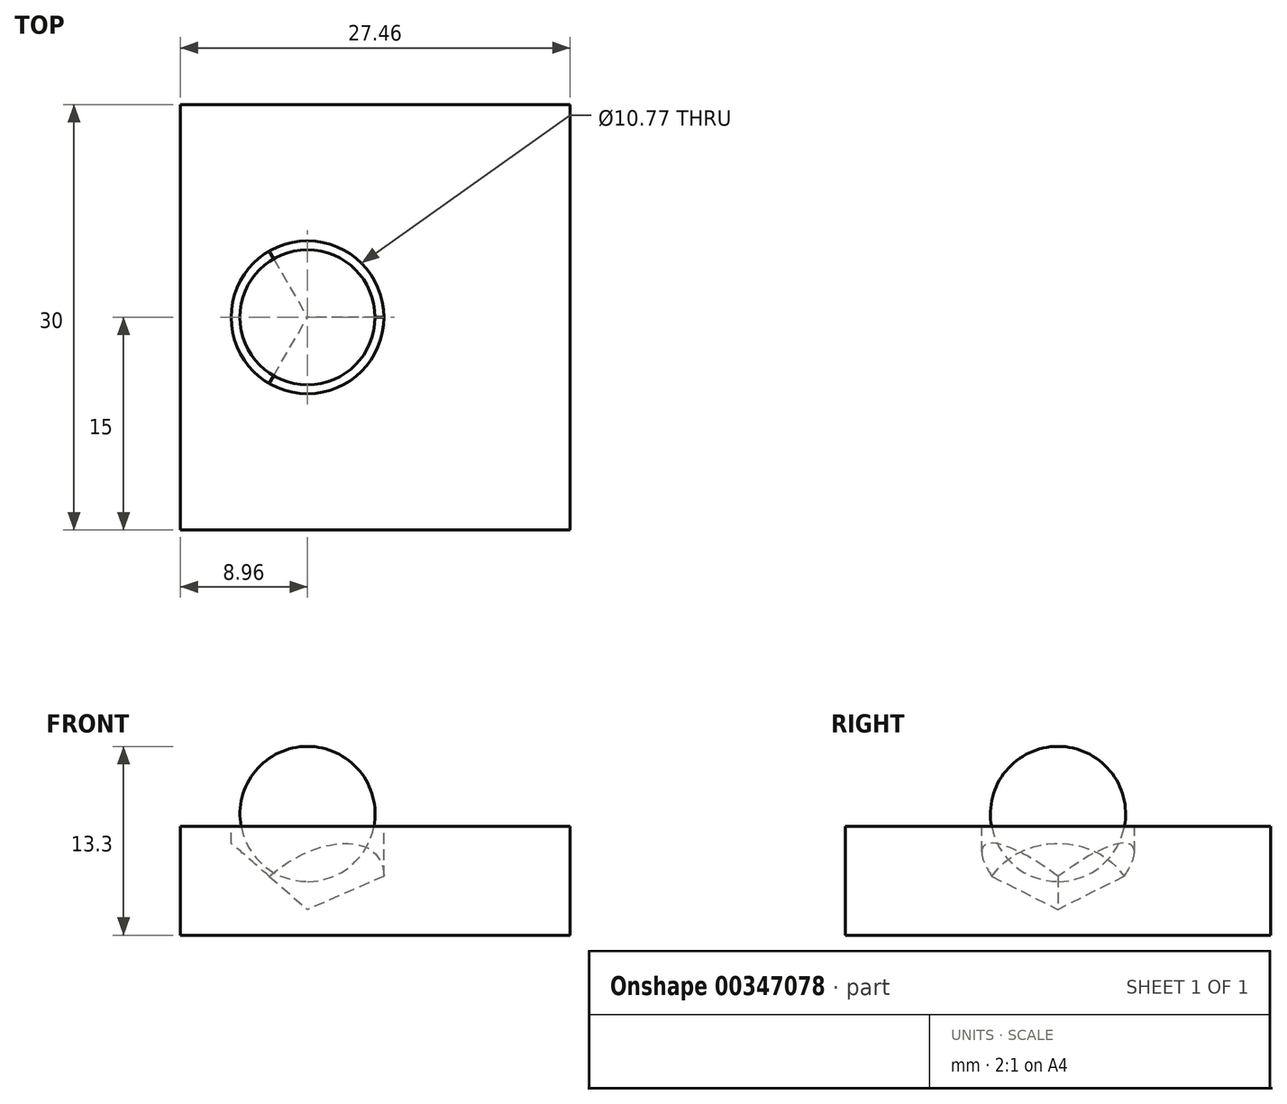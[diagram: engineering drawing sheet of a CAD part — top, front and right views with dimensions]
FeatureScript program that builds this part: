
annotation { "Feature Type Name" : "Feature", "Feature Type Description" : "" }
export const myFeature = defineFeature(function(context is Context, id is Id, definition is map)
    precondition{}
    {
        {
            var Q0;
            Q0=qCreatedBy(makeId("Front.planeOp"),FACE);
            var sketch = newSketch(context, id + "F0", { "sketchPlane" : qUnion([Q0])});
            skLineSegment(sketch, "E0", {"start": v(-6.74, 4.43) * mm, "end": v(0, -2.3) * mm});
            skLineSegment(sketch, "E1", {"start": v(-6.74, 4.43) * mm, "end": v(0, 4.43) * mm});
            skLineSegment(sketch, "E2", {"start": v(0, 4.43) * mm, "end": v(0, -0.33) * mm});
            skPoint(sketch, "E3", {"position": v(-4.76, 4.43) * mm});
            skLineSegment(sketch, "E4", {"start": v(0, -0.33) * mm, "end": v(0, -2.3) * mm});
            skLineSegment(sketch, "E5", {"start": v(0, 4.43) * mm, "end": v(0, 9.2) * mm});
            skLineSegment(sketch, "E6", {"start": v(0, 9.2) * mm, "end": v(0, 12.63) * mm, "construction": true});
            skArc(sketch, "E7", {"start": v(0, 9.2) * mm, "mid": v(-4.76, 4.43) * mm, "end": v(0, -0.33) * mm, "construction": true});
            skArc(sketch, "E8", {"start": v(0, -0.33) * mm, "mid": v(4.76, 4.43) * mm, "end": v(0, 9.2) * mm});
            skSolve(sketch);
        }
        {
            var Q0;
            Q0=qCreatedBy(makeId("Front.planeOp"),FACE);
            var sketch = newSketch(context, id + "F1", { "sketchPlane" : qUnion([Q0])});
            skLineSegment(sketch, "E9.bottom", {"start": v(-8.96, 3.55) * mm, "end": v(18.5, 3.55) * mm});
            skLineSegment(sketch, "E9.top", {"start": v(-8.96, -4.11) * mm, "end": v(18.5, -4.11) * mm});
            skLineSegment(sketch, "E9.left", {"start": v(-8.96, 3.55) * mm, "end": v(-8.96, -4.11) * mm});
            skLineSegment(sketch, "E9.right", {"start": v(18.5, 3.55) * mm, "end": v(18.5, -4.11) * mm});
            skLineSegment(sketch, "E10.0", {"start": v(-6.74, 4.43) * mm, "end": v(0, 4.43) * mm, "construction": true});
            skSolve(sketch);
        }
        {
            var Q0;
            Q0 = qSketchRegion(id + "F1", true);
            extrude(context, id + "F2", {"entities" : qUnion([Q0]), "depth" : 30 * mm, "symmetric" : true});
        }
        {
            var Q0;
            Q0=makeQuery(id+"F2.opExtrude","SWEPT_FACE",FACE,{"disambiguationData":[OSD([sQuery(id+"F1.wireOp",EDGE,"E9.bottom")])]});
            var sketch = newSketch(context, id + "F3", { "sketchPlane" : qUnion([Q0])});
            skPoint(sketch, "E11.0", {"position": v(-6.74, 0) * mm});
            skCircle(sketch, "E12.cCircle", {"center": v(0, 0) * mm, "radius": 6.74 * mm, "construction": true});
            skLineSegment(sketch, "E12.0", {"start": v(-6.74, -11.67) * mm, "end": v(-6.74, 11.67) * mm});
            skLineSegment(sketch, "E12.1", {"start": v(-6.74, 11.67) * mm, "end": v(13.47, 0) * mm});
            skLineSegment(sketch, "E12.2", {"start": v(13.47, 0) * mm, "end": v(-6.74, -11.67) * mm});
            skSolve(sketch);
        }
        {
            var Q1;
            Q1=makeQuery(id+"F3.imprint","IMPRINT",FACE,{"disambiguationData":[TD([[makeQuery(id+"F3.imprint","IMPRINT",EDGE,{"derivedFrom":sQuery(id+"F3.wireOp",EDGE,"E12.0")}),-1.0]])]});
            var Q2;
            Q2=sQuery(id+"F0.wireOp",VERTEX,"E4.end");
            loft(context, id + "F4", {"operationType" : NewBodyOperationType.REMOVE, "sheetProfilesArray" : [{ "sheetProfileEntities" : qUnion([Q1]) }, { "sheetProfileEntities" : qUnion([Q2]) }]});
        }
        {
            var Q0;
            Q0=makeQuery(id+"F2.opExtrude","SWEPT_FACE",FACE,{"disambiguationData":[OSD([sQuery(id+"F1.wireOp",EDGE,"E9.bottom")])]});
            var sketch = newSketch(context, id + "F5", { "sketchPlane" : qUnion([Q0])});
            skPoint(sketch, "E13.0", {"position": v(0, 0) * mm});
            skCircle(sketch, "E14", {"center": v(0, 0) * mm, "radius": 5.38 * mm});
            skLineSegment(sketch, "E15.0", {"start": v(-6.74, -11.67) * mm, "end": v(-6.74, 11.67) * mm});
            skLineSegment(sketch, "E16.0", {"start": v(-6.74, 11.67) * mm, "end": v(13.47, 0) * mm});
            skLineSegment(sketch, "E17.0", {"start": v(13.47, 0) * mm, "end": v(-6.74, -11.67) * mm});
            skSolve(sketch);
        }
        {
            var Q0;
            Q0 = qSketchRegion(id + "F5", true);
            extrude(context, id + "F6", {"entities" : qUnion([Q0]), "operationType" : NewBodyOperationType.ADD, "endBound" : BoundingType.UP_TO_NEXT, "oppositeDirection" : true, "depth" : 25 * mm});
        }
        {
            var Q0;
            Q0=makeQuery(id+"F0.imprint","IMPRINT",FACE,{"disambiguationData":[TD([[makeQuery(id+"F0.imprint","IMPRINT",EDGE,{"derivedFrom":sQuery(id+"F0.wireOp",EDGE,"E2")}),1.0]])]});
            var Q1;
            Q1=sQuery(id+"F0.wireOp",EDGE,"E6");
            revolve(context, id + "F7", {"entities" : qUnion([Q0]), "axis" : qUnion([Q1]), "revolveType" : RevolveType.FULL});
        }
    });
